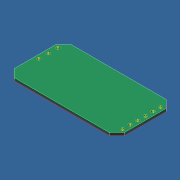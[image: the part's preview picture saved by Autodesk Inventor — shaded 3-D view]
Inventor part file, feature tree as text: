
AUTODESK INVENTOR PART (.ipt)
format: ipt  version: unknown  size: 248,832 bytes
history: native  units: mm
features: sketch x14, hole x2, extrude x1
ambient origin geometry x8: Origin, YZ Plane, XZ Plane, XY Plane, X Axis, Y Axis, Z Axis, Center Point
feature tree (17):
  extrude  "Выдавливание1"  Depth=58.0mm
  hole  "Отверстие1"  [1 undecoded]
  sketch  "Эскиз3"
  sketch  "Эскиз4"
  sketch  "Эскиз5"
  sketch  "Эскиз6"
  sketch  "Эскиз7"
  sketch  "Эскиз8"
  sketch  "Эскиз9"
  sketch  "Эскиз10"
  sketch  "Эскиз11"
  hole  "Отверстие2"  [1 undecoded]
  sketch  "Эскиз14"
  sketch  "Эскиз15"
  sketch  "Эскиз1"
  sketch  "Эскиз2"
  sketch  "Эскиз13"
note: 2 required parameter values undecoded (feature->parameter linkage not recoverable at this tier; creation-order binding heuristic only, values carry confidence <= 0.55)
